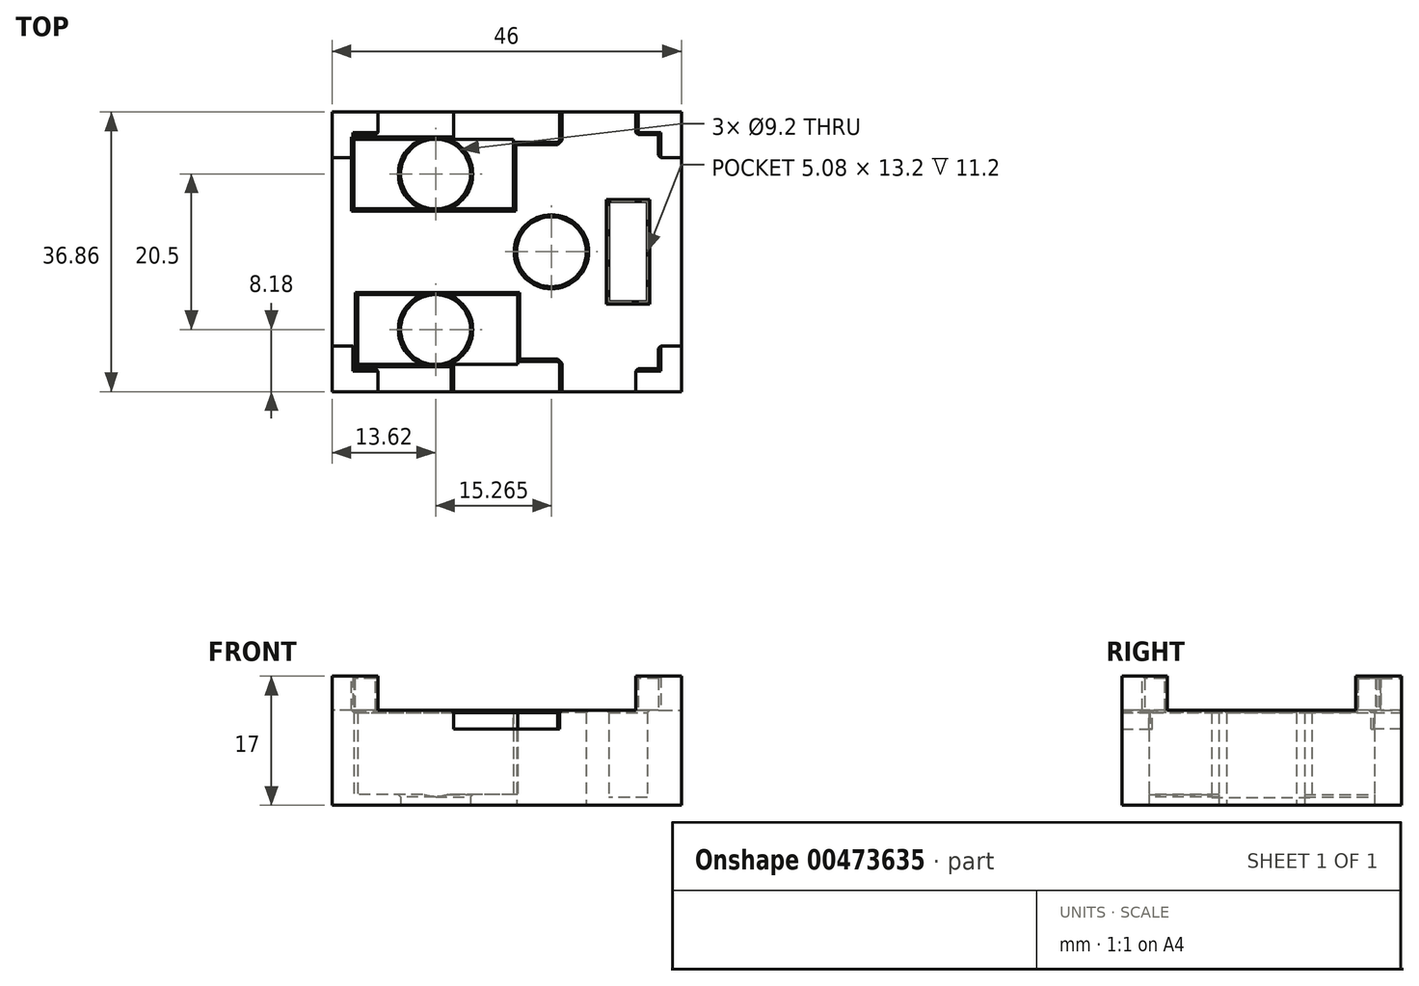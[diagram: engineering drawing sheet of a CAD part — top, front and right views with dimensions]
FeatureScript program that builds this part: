
annotation { "Feature Type Name" : "Feature", "Feature Type Description" : "" }
export const myFeature = defineFeature(function(context is Context, id is Id, definition is map)
    precondition{}
    {
        {
            var Q0;
            Q0=qCreatedBy(makeId("Top.planeOp"),FACE);
            var sketch = newSketch(context, id + "F0", { "sketchPlane" : qUnion([Q0])});
            skLineSegment(sketch, "E0.bottom", {"start": v(20, 15.43) * mm, "end": v(-20, 15.43) * mm});
            skLineSegment(sketch, "E0.top", {"start": v(20, -15.43) * mm, "end": v(-20, -15.43) * mm});
            skLineSegment(sketch, "E0.left", {"start": v(20, 15.43) * mm, "end": v(20, -15.43) * mm});
            skLineSegment(sketch, "E0.right", {"start": v(-20, 15.43) * mm, "end": v(-20, -15.43) * mm});
            skPoint(sketch, "E0.middle", {"position": v(0, 0) * mm});
            skLineSegment(sketch, "E1.0", {"start": v(-23, 18.43) * mm, "end": v(-23, -18.43) * mm});
            skLineSegment(sketch, "E1.1", {"start": v(23, 18.43) * mm, "end": v(-23, 18.43) * mm});
            skLineSegment(sketch, "E1.2", {"start": v(23, 18.43) * mm, "end": v(23, -18.43) * mm});
            skLineSegment(sketch, "E1.3", {"start": v(23, -18.43) * mm, "end": v(-23, -18.43) * mm});
            skLineSegment(sketch, "E2", {"start": v(-17, 15.43) * mm, "end": v(-17, 18.43) * mm});
            skLineSegment(sketch, "E3", {"start": v(17, 15.43) * mm, "end": v(17, 18.43) * mm});
            skLineSegment(sketch, "E4", {"start": v(20, 12.43) * mm, "end": v(23, 12.43) * mm});
            skLineSegment(sketch, "E5", {"start": v(-20, 12.43) * mm, "end": v(-23, 12.43) * mm});
            skLineSegment(sketch, "E6.MirrorCS", {"start": v(-20, -12.43) * mm, "end": v(-23, -12.43) * mm});
            skLineSegment(sketch, "E7.MirrorCS", {"start": v(-17, -15.43) * mm, "end": v(-17, -18.43) * mm});
            skLineSegment(sketch, "E8.MirrorCS", {"start": v(17, -15.43) * mm, "end": v(17, -18.43) * mm});
            skLineSegment(sketch, "E9.MirrorCS", {"start": v(20, -12.43) * mm, "end": v(23, -12.43) * mm});
            skLineSegment(sketch, "E10", {"start": v(-15, 10.25) * mm, "end": v(6.7, 10.25) * mm, "construction": true});
            skCircle(sketch, "E11", {"center": v(-17, 10.25) * mm, "radius": 1.03 * mm, "construction": true});
            skCircle(sketch, "E12", {"center": v(-11.92, 10.25) * mm, "radius": 1.03 * mm, "construction": true});
            skCircle(sketch, "E13", {"center": v(-6.84, 10.25) * mm, "radius": 1.03 * mm, "construction": true});
            skCircle(sketch, "E14", {"center": v(-1.76, 10.25) * mm, "radius": 1.03 * mm, "construction": true});
            skLineSegment(sketch, "E15.MirrorCS", {"start": v(-15, -10.25) * mm, "end": v(6.7, -10.25) * mm, "construction": true});
            skLineSegment(sketch, "E16.bottom", {"start": v(0.87, 5.65) * mm, "end": v(-19.63, 5.65) * mm});
            skLineSegment(sketch, "E16.top", {"start": v(0.87, 14.85) * mm, "end": v(-19.63, 14.85) * mm});
            skLineSegment(sketch, "E16.left", {"start": v(0.87, 5.65) * mm, "end": v(0.87, 14.85) * mm});
            skLineSegment(sketch, "E16.right", {"start": v(-19.63, 5.65) * mm, "end": v(-19.63, 14.85) * mm, "construction": true});
            skPoint(sketch, "E16.middle", {"position": v(-9.38, 10.25) * mm});
            skLineSegment(sketch, "E17.MirrorCS", {"start": v(0.87, -5.65) * mm, "end": v(0.87, -14.85) * mm, "construction": true});
            skLineSegment(sketch, "E18.MirrorCS", {"start": v(0.87, -14.85) * mm, "end": v(-19.63, -14.85) * mm});
            skLineSegment(sketch, "E19.MirrorCS", {"start": v(0.87, -5.65) * mm, "end": v(-19.63, -5.65) * mm});
            skLineSegment(sketch, "E20.MirrorCS", {"start": v(-19.63, -5.65) * mm, "end": v(-19.63, -14.85) * mm});
            skLineSegment(sketch, "E21", {"start": v(17.25, 11) * mm, "end": v(17.25, -11.34) * mm, "construction": true});
            skLineSegment(sketch, "E22.bottom", {"start": v(18.52, -6.6) * mm, "end": v(13.44, -6.6) * mm});
            skLineSegment(sketch, "E22.top", {"start": v(18.52, 6.6) * mm, "end": v(13.44, 6.6) * mm});
            skLineSegment(sketch, "E22.left", {"start": v(18.52, -6.6) * mm, "end": v(18.52, 6.6) * mm});
            skLineSegment(sketch, "E22.right", {"start": v(13.44, -6.6) * mm, "end": v(13.44, 6.6) * mm});
            skPoint(sketch, "E22.middle", {"position": v(15.98, 0) * mm});
            skLineSegment(sketch, "E23.bottom", {"start": v(-19.63, 14.85) * mm, "end": v(-20.18, 14.85) * mm});
            skLineSegment(sketch, "E23.top", {"start": v(-19.63, 5.65) * mm, "end": v(-20.18, 5.65) * mm});
            skLineSegment(sketch, "E23.left", {"start": v(-19.63, 14.85) * mm, "end": v(-19.63, 5.65) * mm, "construction": true});
            skLineSegment(sketch, "E23.right", {"start": v(-20.18, 14.85) * mm, "end": v(-20.18, 5.65) * mm});
            skLineSegment(sketch, "E24.bottom", {"start": v(0.87, -5.65) * mm, "end": v(1.42, -5.65) * mm});
            skLineSegment(sketch, "E24.top", {"start": v(0.87, -14.85) * mm, "end": v(1.42, -14.85) * mm});
            skLineSegment(sketch, "E24.right", {"start": v(1.42, -5.65) * mm, "end": v(1.42, -14.85) * mm});
            skCircle(sketch, "E25", {"center": v(-9.38, 10.25) * mm, "radius": 4.6 * mm});
            skCircle(sketch, "E26.MirrorC", {"center": v(-9.38, -10.25) * mm, "radius": 4.6 * mm});
            skCircle(sketch, "E27", {"center": v(5.89, 0) * mm, "radius": 4.6 * mm});
            skLineSegment(sketch, "E28", {"start": v(0.87, 5.65) * mm, "end": v(5.89, 0) * mm, "construction": true});
            skLineSegment(sketch, "E29", {"start": v(5.89, 0) * mm, "end": v(13.44, 0) * mm, "construction": true});
            skLineSegment(sketch, "E30", {"start": v(-7, 18.43) * mm, "end": v(-7, 15.43) * mm});
            skLineSegment(sketch, "E31.MirrorCS", {"start": v(7, 18.43) * mm, "end": v(7, 15.43) * mm});
            skLineSegment(sketch, "E32.MirrorCS", {"start": v(-7, -18.43) * mm, "end": v(-7, -15.43) * mm});
            skLineSegment(sketch, "E33.MirrorCS", {"start": v(7, -18.43) * mm, "end": v(7, -15.43) * mm});
            skSolve(sketch);
        }
        {
            var Q0;
            Q0=makeQuery(id+"F0.imprint","IMPRINT",FACE,{"disambiguationData":[TD([[makeQuery(id+"F0.imprint","IMPRINT",EDGE,{"derivedFrom":sQuery(id+"F0.wireOp",EDGE,"E16.bottom")}),1.0]])]});
            var Q1;
            {var subQ0=sQuery(id+"F0.wireOp",EDGE,"E2");Q1=makeQuery(id+"F0.imprint","IMPRINT",FACE,{"disambiguationData":[TD([[makeQuery(id+"F0.imprint","IMPRINT",EDGE,{"derivedFrom":subQ0}),-1.0]])]});}
            var Q2;
            {var subQ0=sQuery(id+"F0.wireOp",EDGE,"E6.MirrorCS");Q2=makeQuery(id+"F0.imprint","IMPRINT",FACE,{"disambiguationData":[TD([[makeQuery(id+"F0.imprint","IMPRINT",EDGE,{"derivedFrom":subQ0}),-1.0]])]});}
            var Q3;
            {var subQ0=sQuery(id+"F0.wireOp",EDGE,"E7.MirrorCS");Q3=makeQuery(id+"F0.imprint","IMPRINT",FACE,{"disambiguationData":[TD([[makeQuery(id+"F0.imprint","IMPRINT",EDGE,{"derivedFrom":subQ0}),1.0]])]});}
            var Q4;
            {var subQ0=sQuery(id+"F0.wireOp",EDGE,"E4");Q4=makeQuery(id+"F0.imprint","IMPRINT",FACE,{"disambiguationData":[TD([[makeQuery(id+"F0.imprint","IMPRINT",EDGE,{"derivedFrom":subQ0}),-1.0]])]});}
            var Q5;
            {var subQ0=sQuery(id+"F0.wireOp",EDGE,"E8.MirrorCS");Q5=makeQuery(id+"F0.imprint","IMPRINT",FACE,{"disambiguationData":[TD([[makeQuery(id+"F0.imprint","IMPRINT",EDGE,{"derivedFrom":subQ0}),-1.0]])]});}
            var Q6;
            {var subQ0=sQuery(id+"F0.wireOp",EDGE,"E3");Q6=makeQuery(id+"F0.imprint","IMPRINT",FACE,{"disambiguationData":[TD([[makeQuery(id+"F0.imprint","IMPRINT",EDGE,{"derivedFrom":subQ0}),1.0]])]});}
            var Q7;
            {var subQ0=sQuery(id+"F0.wireOp",EDGE,"E32.MirrorCS");Q7=makeQuery(id+"F0.imprint","IMPRINT",FACE,{"disambiguationData":[TD([[makeQuery(id+"F0.imprint","IMPRINT",EDGE,{"derivedFrom":subQ0}),-1.0]])]});}
            var Q8;
            {var subQ0=sQuery(id+"F0.wireOp",EDGE,"E30");Q8=makeQuery(id+"F0.imprint","IMPRINT",FACE,{"disambiguationData":[TD([[makeQuery(id+"F0.imprint","IMPRINT",EDGE,{"derivedFrom":subQ0}),1.0]])]});}
            extrude(context, id + "F1", {"entities" : qUnion([Q0, Q1, Q2, Q3, Q4, Q5, Q6, Q7, Q8]), "depth" : (15 - 2.5) * mm, "offsetDistance" : 25 * mm});
        }
        {
            var Q0;
            {var subQ5=sQuery(id+"F0.wireOp",EDGE,"E0.right");var subQ11=makeQuery(id+"F0.imprint","INTERSECT",VERTEX,{"derivedFrom":[subQ5,sQuery(id+"F0.wireOp",EDGE,"E5")]});Q0=makeQuery(id+"F0.imprint","IMPRINT",FACE,{"disambiguationData":[TD([[makeQuery(id+"F0.imprint","IMPRINT",EDGE,{"disambiguationData":[TD([[subQ11,1.0]])],"derivedFrom":subQ5}),1.0]])]});}
            var Q1;
            {var subQ0=sQuery(id+"F0.wireOp",EDGE,"E5");var subQ1=sQuery(id+"F0.wireOp",EDGE,"E0.right");var subQ2=makeQuery(id+"F0.imprint","INTERSECT",VERTEX,{"derivedFrom":[subQ1,subQ0]});Q1=makeQuery(id+"F0.imprint","IMPRINT",FACE,{"disambiguationData":[TD([[makeQuery(id+"F0.imprint","IMPRINT",EDGE,{"disambiguationData":[TD([[subQ2,-1.0]])],"derivedFrom":subQ1}),-1.0]])]});}
            var Q2;
            {var subQ0=sQuery(id+"F0.wireOp",EDGE,"E16.left");Q2=makeQuery(id+"F0.imprint","IMPRINT",FACE,{"disambiguationData":[TD([[makeQuery(id+"F0.imprint","IMPRINT",EDGE,{"derivedFrom":subQ0}),1.0]])]});}
            var Q3;
            {var subQ0=sQuery(id+"F0.wireOp",EDGE,"E20.MirrorCS");Q3=makeQuery(id+"F0.imprint","IMPRINT",FACE,{"disambiguationData":[TD([[makeQuery(id+"F0.imprint","IMPRINT",EDGE,{"derivedFrom":subQ0}),1.0]])]});}
            var Q4;
            {var subQ1=sQuery(id+"F0.wireOp",EDGE,"E24.bottom");Q4=makeQuery(id+"F0.imprint","IMPRINT",FACE,{"disambiguationData":[TD([[makeQuery(id+"F0.imprint","IMPRINT",EDGE,{"derivedFrom":subQ1}),-1.0]])]});}
            var Q5;
            {var subQ0=sQuery(id+"F0.wireOp",EDGE,"E5");var subQ1=sQuery(id+"F0.wireOp",EDGE,"E0.right");var subQ2=makeQuery(id+"F0.imprint","INTERSECT",VERTEX,{"derivedFrom":[subQ1,subQ0]});Q5=makeQuery(id+"F0.imprint","IMPRINT",FACE,{"disambiguationData":[TD([[makeQuery(id+"F0.imprint","IMPRINT",EDGE,{"disambiguationData":[TD([[subQ2,1.0]])],"derivedFrom":subQ1}),-1.0]])]});}
            extrude(context, id + "F2", {"entities" : qUnion([Q0, Q1, Q2, Q3, Q4, Q5]), "operationType" : NewBodyOperationType.ADD, "depth" : (15 - 13.6) * mm, "offsetDistance" : 25 * mm});
        }
        {
            var Q0;
            Q0=makeQuery(id+"F0.imprint","IMPRINT",FACE,{"disambiguationData":[TD([[makeQuery(id+"F0.imprint","IMPRINT",EDGE,{"derivedFrom":sQuery(id+"F0.wireOp",EDGE,"E22.bottom")}),-1.0]])]});
            extrude(context, id + "F3", {"entities" : qUnion([Q0]), "operationType" : NewBodyOperationType.ADD, "depth" : (15 - 14) * mm, "offsetDistance" : 25 * mm});
        }
        {
            var Q0;
            {var subQ3=sQuery(id+"F0.wireOp",EDGE,"E6.MirrorCS");Q0=makeQuery(id+"F0.imprint","IMPRINT",FACE,{"disambiguationData":[TD([[makeQuery(id+"F0.imprint","IMPRINT",EDGE,{"derivedFrom":subQ3}),1.0]])]});}
            var Q1;
            {var subQ4=sQuery(id+"F0.wireOp",EDGE,"E8.MirrorCS");Q1=makeQuery(id+"F0.imprint","IMPRINT",FACE,{"disambiguationData":[TD([[makeQuery(id+"F0.imprint","IMPRINT",EDGE,{"derivedFrom":subQ4}),1.0]])]});}
            var Q2;
            {var subQ3=sQuery(id+"F0.wireOp",EDGE,"E3");Q2=makeQuery(id+"F0.imprint","IMPRINT",FACE,{"disambiguationData":[TD([[makeQuery(id+"F0.imprint","IMPRINT",EDGE,{"derivedFrom":subQ3}),-1.0]])]});}
            var Q3;
            {var subQ3=sQuery(id+"F0.wireOp",EDGE,"E2");Q3=makeQuery(id+"F0.imprint","IMPRINT",FACE,{"disambiguationData":[TD([[makeQuery(id+"F0.imprint","IMPRINT",EDGE,{"derivedFrom":subQ3}),1.0]])]});}
            extrude(context, id + "F4", {"entities" : qUnion([Q0, Q1, Q2, Q3]), "operationType" : NewBodyOperationType.ADD, "depth" : 17 * mm, "offsetDistance" : 25 * mm});
        }
        {
            var Q0;
            Q0=makeQuery(id+"F1.opExtrude","CAP_FACE",FACE,{"disambiguationData":[OSD([sQuery(id+"F0.wireOp",EDGE,"E0.bottom"),sQuery(id+"F0.wireOp",EDGE,"E0.top"),sQuery(id+"F0.wireOp",EDGE,"E0.left"),sQuery(id+"F0.wireOp",EDGE,"E0.right"),sQuery(id+"F0.wireOp",EDGE,"E16.bottom"),sQuery(id+"F0.wireOp",EDGE,"E16.top"),sQuery(id+"F0.wireOp",EDGE,"E16.left"),sQuery(id+"F0.wireOp",EDGE,"E18.MirrorCS"),sQuery(id+"F0.wireOp",EDGE,"E19.MirrorCS"),sQuery(id+"F0.wireOp",EDGE,"E20.MirrorCS"),sQuery(id+"F0.wireOp",EDGE,"E22.bottom"),sQuery(id+"F0.wireOp",EDGE,"E22.top"),sQuery(id+"F0.wireOp",EDGE,"E22.left"),sQuery(id+"F0.wireOp",EDGE,"E22.right"),sQuery(id+"F0.wireOp",EDGE,"E23.bottom"),sQuery(id+"F0.wireOp",EDGE,"E23.top"),sQuery(id+"F0.wireOp",EDGE,"E24.bottom"),sQuery(id+"F0.wireOp",EDGE,"E24.top"),sQuery(id+"F0.wireOp",EDGE,"E24.right")])],"isStart":false});
            var sketch = newSketch(context, id + "F5", { "sketchPlane" : qUnion([Q0])});
            skLineSegment(sketch, "E34", {"start": v(0.87, 14.43) * mm, "end": v(20, 14.43) * mm});
            skLineSegment(sketch, "E35", {"start": v(1.42, -14.43) * mm, "end": v(20, -14.43) * mm});
            skLineSegment(sketch, "E36", {"start": v(-17, -5.65) * mm, "end": v(-17, 5.65) * mm});
            skLineSegment(sketch, "E37.0", {"start": v(7, -18.43) * mm, "end": v(7, -15.43) * mm});
            skLineSegment(sketch, "E37.1", {"start": v(-7, -18.43) * mm, "end": v(-7, -15.43) * mm});
            skLineSegment(sketch, "E37.2", {"start": v(7, 18.43) * mm, "end": v(7, 15.43) * mm});
            skLineSegment(sketch, "E37.3", {"start": v(-7, 18.43) * mm, "end": v(-7, 15.43) * mm});
            skLineSegment(sketch, "E38", {"start": v(-7, 15.43) * mm, "end": v(-7, 14.85) * mm});
            skLineSegment(sketch, "E39", {"start": v(7, 15.43) * mm, "end": v(7, 14.43) * mm});
            skLineSegment(sketch, "E40", {"start": v(-7, -15.43) * mm, "end": v(-7, -14.85) * mm});
            skLineSegment(sketch, "E41", {"start": v(7, -15.43) * mm, "end": v(7, -14.43) * mm});
            skSolve(sketch);
        }
        {
            var Q0;
            {var subQ2=sQuery(id+"F5.wireOp",EDGE,"E37.0");Q0=makeQuery(id+"F5.imprint","IMPRINT",FACE,{"disambiguationData":[TD([[makeQuery(id+"F5.imprint","IMPRINT",EDGE,{"derivedFrom":subQ2}),1.0]])]});}
            var Q1;
            {var subQ2=sQuery(id+"F5.wireOp",EDGE,"E37.2");Q1=makeQuery(id+"F5.imprint","IMPRINT",FACE,{"disambiguationData":[TD([[makeQuery(id+"F5.imprint","IMPRINT",EDGE,{"derivedFrom":subQ2}),-1.0]])]});}
            extrude(context, id + "F6", {"entities" : qUnion([Q0, Q1]), "operationType" : NewBodyOperationType.REMOVE, "oppositeDirection" : true, "depth" : 2.5 * mm, "offsetDistance" : 25 * mm});
        }
        {
            var Q0;
            Q0=makeQuery(id+"F1.opExtrude","CAP_EDGE",EDGE,{"disambiguationData":[OSD([sQuery(id+"F0.wireOp",EDGE,"E16.top"),sQuery(id+"F0.wireOp",EDGE,"E23.bottom")])],"isStart":false});
            var Q1;
            Q1=makeQuery(id+"F1.opExtrude","CAP_EDGE",EDGE,{"disambiguationData":[OSD([sQuery(id+"F0.wireOp",EDGE,"E23.right")])],"isStart":false});
            var Q2;
            Q2=makeQuery(id+"F1.opExtrude","CAP_EDGE",EDGE,{"disambiguationData":[OSD([sQuery(id+"F0.wireOp",EDGE,"E16.bottom"),sQuery(id+"F0.wireOp",EDGE,"E23.top")])],"isStart":false});
            var Q3;
            Q3=makeQuery(id+"F6.boolean.opBoolean","COPY",EDGE,{"derivedFrom":makeQuery(id+"F6.opExtrude","CAP_EDGE",EDGE,{"disambiguationData":[OSD([sQuery(id+"F0.wireOp",EDGE,"E16.bottom"),sQuery(id+"F0.wireOp",EDGE,"E23.top")])],"isStart":false})});
            var Q4;
            Q4=makeQuery(id+"F6.boolean.opBoolean","COPY",EDGE,{"derivedFrom":makeQuery(id+"F6.opExtrude","CAP_EDGE",EDGE,{"disambiguationData":[OSD([sQuery(id+"F0.wireOp",EDGE,"E16.left")])],"isStart":false})});
            var Q5;
            Q5=makeQuery(id+"F6.boolean.opBoolean","COPY",EDGE,{"derivedFrom":makeQuery(id+"F6.opExtrude","CAP_EDGE",EDGE,{"disambiguationData":[OSD([sQuery(id+"F0.wireOp",EDGE,"E22.left")])],"isStart":false})});
            var Q6;
            Q6=makeQuery(id+"F6.boolean.opBoolean","COPY",EDGE,{"derivedFrom":makeQuery(id+"F6.opExtrude","CAP_EDGE",EDGE,{"disambiguationData":[OSD([sQuery(id+"F0.wireOp",EDGE,"E22.top")])],"isStart":false})});
            var Q7;
            Q7=makeQuery(id+"F6.boolean.opBoolean","COPY",EDGE,{"derivedFrom":makeQuery(id+"F6.opExtrude","CAP_EDGE",EDGE,{"disambiguationData":[OSD([sQuery(id+"F0.wireOp",EDGE,"E22.right")])],"isStart":false})});
            var Q8;
            Q8=makeQuery(id+"F6.boolean.opBoolean","COPY",EDGE,{"derivedFrom":makeQuery(id+"F6.opExtrude","CAP_EDGE",EDGE,{"disambiguationData":[OSD([sQuery(id+"F0.wireOp",EDGE,"E22.bottom")])],"isStart":false})});
            var Q9;
            Q9=makeQuery(id+"F6.boolean.opBoolean","COPY",EDGE,{"derivedFrom":makeQuery(id+"F6.opExtrude","CAP_EDGE",EDGE,{"disambiguationData":[OSD([sQuery(id+"F0.wireOp",EDGE,"E19.MirrorCS"),sQuery(id+"F0.wireOp",EDGE,"E24.bottom")])],"isStart":false})});
            var Q10;
            Q10=makeQuery(id+"F1.opExtrude","CAP_EDGE",EDGE,{"disambiguationData":[OSD([sQuery(id+"F0.wireOp",EDGE,"E19.MirrorCS"),sQuery(id+"F0.wireOp",EDGE,"E24.bottom")])],"isStart":false});
            var Q11;
            Q11=makeQuery(id+"F1.opExtrude","CAP_EDGE",EDGE,{"disambiguationData":[OSD([sQuery(id+"F0.wireOp",EDGE,"E20.MirrorCS")])],"isStart":false});
            var Q12;
            Q12=makeQuery(id+"F1.opExtrude","CAP_EDGE",EDGE,{"disambiguationData":[OSD([sQuery(id+"F0.wireOp",EDGE,"E18.MirrorCS"),sQuery(id+"F0.wireOp",EDGE,"E24.top")])],"isStart":false});
            var Q13;
            Q13=makeQuery(id+"F1.opExtrude","CAP_EDGE",EDGE,{"disambiguationData":[OSD([sQuery(id+"F0.wireOp",EDGE,"E24.right")])],"isStart":false});
            var Q14;
            Q14=makeQuery(id+"F6.boolean.opBoolean","COPY",EDGE,{"derivedFrom":makeQuery(id+"F6.opExtrude","CAP_EDGE",EDGE,{"disambiguationData":[OSD([sQuery(id+"F0.wireOp",EDGE,"E24.right")])],"isStart":false})});
            var Q15;
            Q15=makeQuery(id+"F1.opExtrude","CAP_EDGE",EDGE,{"disambiguationData":[OSD([sQuery(id+"F0.wireOp",EDGE,"E16.left")])],"isStart":false});
            var Q16;
            Q16=makeQuery(id+"F4.opExtrude","CAP_EDGE",EDGE,{"disambiguationData":[OSD([sQuery(id+"F0.wireOp",EDGE,"E23.right")])],"isStart":false});
            var Q17;
            Q17=makeQuery(id+"F4.opExtrude","CAP_EDGE",EDGE,{"disambiguationData":[OSD([sQuery(id+"F0.wireOp",EDGE,"E23.bottom")])],"isStart":false});
            var Q18;
            Q18=makeQuery(id+"F4.opExtrude","SWEPT_EDGE",EDGE,{"disambiguationData":[OSD([sQuery(id+"F0.wireOp",EDGE,"E0.bottom"),sQuery(id+"F0.wireOp",EDGE,"E3")])]});
            var Q19;
            {var subQ0=sQuery(id+"F0.wireOp",EDGE,"E4");var subQ1=sQuery(id+"F0.wireOp",EDGE,"E0.left");Q19=makeQuery(id+"F6.boolean.opBoolean","MERGE",EDGE,{"derivedFrom":[makeQuery(id+"F4.opExtrude","SWEPT_EDGE",EDGE,{"disambiguationData":[OSD([subQ1,subQ0])]})],"fromTools":[makeQuery(id+"F6.opExtrude","SWEPT_EDGE",EDGE,{"disambiguationData":[OSD([subQ1,subQ0])]})]});}
            var Q20;
            Q20=makeQuery(id+"F4.opExtrude","SWEPT_EDGE",EDGE,{"disambiguationData":[OSD([sQuery(id+"F0.wireOp",EDGE,"E5"),sQuery(id+"F0.wireOp",EDGE,"E23.right")])]});
            var Q21;
            Q21=makeQuery(id+"F4.opExtrude","SWEPT_EDGE",EDGE,{"disambiguationData":[OSD([sQuery(id+"F0.wireOp",EDGE,"E0.bottom"),sQuery(id+"F0.wireOp",EDGE,"E2")])]});
            var Q22;
            Q22=makeQuery(id+"F4.opExtrude","SWEPT_EDGE",EDGE,{"disambiguationData":[OSD([sQuery(id+"F0.wireOp",EDGE,"E0.right"),sQuery(id+"F0.wireOp",EDGE,"E6.MirrorCS")])]});
            var Q23;
            Q23=makeQuery(id+"F4.opExtrude","SWEPT_EDGE",EDGE,{"disambiguationData":[OSD([sQuery(id+"F0.wireOp",EDGE,"E0.top"),sQuery(id+"F0.wireOp",EDGE,"E7.MirrorCS")])]});
            var Q24;
            {var subQ0=sQuery(id+"F0.wireOp",EDGE,"E9.MirrorCS");var subQ1=sQuery(id+"F0.wireOp",EDGE,"E0.left");Q24=makeQuery(id+"F6.boolean.opBoolean","MERGE",EDGE,{"derivedFrom":[makeQuery(id+"F4.opExtrude","SWEPT_EDGE",EDGE,{"disambiguationData":[OSD([subQ1,subQ0])]})],"fromTools":[makeQuery(id+"F6.opExtrude","SWEPT_EDGE",EDGE,{"disambiguationData":[OSD([subQ1,subQ0])]})]});}
            var Q25;
            Q25=makeQuery(id+"F4.opExtrude","SWEPT_EDGE",EDGE,{"disambiguationData":[OSD([sQuery(id+"F0.wireOp",EDGE,"E0.top"),sQuery(id+"F0.wireOp",EDGE,"E8.MirrorCS")])]});
            var Q26;
            {var subQ0=sQuery(id+"F0.wireOp",EDGE,"E25");Q26=makeQuery(id+"F2.opExtrude","CAP_EDGE",EDGE,{"disambiguationData":[OSD([subQ0]),TDD([makeQuery(id+"F0.imprint","IMPRINT",EDGE,{"disambiguationData":[TD([[makeQuery(id+"F0.imprint","INTERSECT",VERTEX,{"derivedFrom":[sQuery(id+"F0.wireOp",EDGE,"E16.bottom"),subQ0]}),1.0]])],"derivedFrom":subQ0})])],"isStart":false});}
            var Q27;
            {var subQ0=sQuery(id+"F0.wireOp",EDGE,"E26.MirrorC");Q27=makeQuery(id+"F2.opExtrude","CAP_EDGE",EDGE,{"disambiguationData":[OSD([subQ0]),TDD([makeQuery(id+"F0.imprint","IMPRINT",EDGE,{"disambiguationData":[TD([[makeQuery(id+"F0.imprint","INTERSECT",VERTEX,{"derivedFrom":[sQuery(id+"F0.wireOp",EDGE,"E18.MirrorCS"),subQ0]}),-1.0]])],"derivedFrom":subQ0})])],"isStart":false});}
            var Q28;
            Q28=makeQuery(id+"F6.boolean.opBoolean","COPY",EDGE,{"derivedFrom":makeQuery(id+"F6.opExtrude","CAP_EDGE",EDGE,{"disambiguationData":[OSD([sQuery(id+"F0.wireOp",EDGE,"E27")])],"isStart":false})});
            var Q29;
            Q29=makeQuery(id+"F6.boolean.opBoolean","COPY",EDGE,{"derivedFrom":makeQuery(id+"F6.opExtrude","CAP_EDGE",EDGE,{"disambiguationData":[OSD([sQuery(id+"F5.wireOp",EDGE,"E35")])],"isStart":true})});
            var Q30;
            Q30=makeQuery(id+"F6.boolean.opBoolean","COPY",EDGE,{"derivedFrom":makeQuery(id+"F6.opExtrude","CAP_EDGE",EDGE,{"disambiguationData":[OSD([sQuery(id+"F5.wireOp",EDGE,"E37.0"),sQuery(id+"F5.wireOp",EDGE,"E41")])],"isStart":true})});
            var Q31;
            Q31=makeQuery(id+"F6.boolean.opBoolean","COPY",EDGE,{"derivedFrom":makeQuery(id+"F6.opExtrude","CAP_EDGE",EDGE,{"disambiguationData":[OSD([sQuery(id+"F5.wireOp",EDGE,"E37.1"),sQuery(id+"F5.wireOp",EDGE,"E40")])],"isStart":true})});
            var Q32;
            Q32=makeQuery(id+"F6.boolean.opBoolean","COPY",EDGE,{"derivedFrom":makeQuery(id+"F6.opExtrude","CAP_EDGE",EDGE,{"disambiguationData":[OSD([sQuery(id+"F5.wireOp",EDGE,"E37.3"),sQuery(id+"F5.wireOp",EDGE,"E38")])],"isStart":true})});
            var Q33;
            Q33=makeQuery(id+"F6.boolean.opBoolean","COPY",EDGE,{"derivedFrom":makeQuery(id+"F6.opExtrude","CAP_EDGE",EDGE,{"disambiguationData":[OSD([sQuery(id+"F5.wireOp",EDGE,"E37.2"),sQuery(id+"F5.wireOp",EDGE,"E39")])],"isStart":true})});
            var Q34;
            Q34=makeQuery(id+"F6.boolean.opBoolean","COPY",EDGE,{"derivedFrom":makeQuery(id+"F6.opExtrude","CAP_EDGE",EDGE,{"disambiguationData":[OSD([sQuery(id+"F5.wireOp",EDGE,"E34")])],"isStart":true})});
            var Q35;
            Q35=makeQuery(id+"F6.boolean.opBoolean","COPY",EDGE,{"derivedFrom":makeQuery(id+"F6.opExtrude","CAP_EDGE",EDGE,{"disambiguationData":[OSD([sQuery(id+"F0.wireOp",EDGE,"E18.MirrorCS"),sQuery(id+"F0.wireOp",EDGE,"E24.top")])],"isStart":false})});
            var Q36;
            Q36=makeQuery(id+"F6.boolean.opBoolean","COPY",EDGE,{"derivedFrom":makeQuery(id+"F6.opExtrude","CAP_EDGE",EDGE,{"disambiguationData":[OSD([sQuery(id+"F0.wireOp",EDGE,"E16.top"),sQuery(id+"F0.wireOp",EDGE,"E23.bottom")])],"isStart":false})});
            var Q37;
            Q37=makeQuery(id+"F6.boolean.opBoolean","COPY",EDGE,{"derivedFrom":makeQuery(id+"F6.opExtrude","SWEPT_EDGE",EDGE,{"disambiguationData":[OSD([sQuery(id+"F0.wireOp",EDGE,"E16.top"),sQuery(id+"F0.wireOp",EDGE,"E23.bottom"),sQuery(id+"F5.wireOp",EDGE,"E38")])]})});
            var Q38;
            Q38=makeQuery(id+"F6.boolean.opBoolean","COPY",EDGE,{"derivedFrom":makeQuery(id+"F6.opExtrude","SWEPT_EDGE",EDGE,{"disambiguationData":[OSD([sQuery(id+"F0.wireOp",EDGE,"E18.MirrorCS"),sQuery(id+"F0.wireOp",EDGE,"E24.top"),sQuery(id+"F5.wireOp",EDGE,"E40")])]})});
            var Q39;
            Q39=makeQuery(id+"F6.boolean.opBoolean","COPY",EDGE,{"derivedFrom":makeQuery(id+"F6.opExtrude","SWEPT_EDGE",EDGE,{"disambiguationData":[OSD([sQuery(id+"F5.wireOp",EDGE,"E35"),sQuery(id+"F5.wireOp",EDGE,"E41")])]})});
            var Q40;
            Q40=makeQuery(id+"F6.boolean.opBoolean","COPY",EDGE,{"derivedFrom":makeQuery(id+"F6.opExtrude","SWEPT_EDGE",EDGE,{"disambiguationData":[OSD([sQuery(id+"F5.wireOp",EDGE,"E34"),sQuery(id+"F5.wireOp",EDGE,"E39")])]})});
            var Q41;
            {var subQ0=sQuery(id+"F0.wireOp",EDGE,"E0.bottom");Q41=makeQuery(id+"F4.opExtrude","CAP_EDGE",EDGE,{"disambiguationData":[OSD([subQ0]),TDD([makeQuery(id+"F0.imprint","IMPRINT",EDGE,{"disambiguationData":[TD([[makeQuery(id+"F0.imprint","INTERSECT",VERTEX,{"derivedFrom":[subQ0,sQuery(id+"F0.wireOp",EDGE,"E0.right")]}),1.0]])],"derivedFrom":subQ0})])],"isStart":false});}
            var Q42;
            Q42=makeQuery(id+"F4.opExtrude","CAP_EDGE",EDGE,{"disambiguationData":[OSD([sQuery(id+"F0.wireOp",EDGE,"E3")])],"isStart":false});
            var Q43;
            {var subQ0=sQuery(id+"F0.wireOp",EDGE,"E0.bottom");Q43=makeQuery(id+"F4.opExtrude","CAP_EDGE",EDGE,{"disambiguationData":[OSD([subQ0]),TDD([makeQuery(id+"F0.imprint","IMPRINT",EDGE,{"disambiguationData":[TD([[makeQuery(id+"F0.imprint","INTERSECT",VERTEX,{"derivedFrom":[subQ0,sQuery(id+"F0.wireOp",EDGE,"E0.left")]}),-1.0]])],"derivedFrom":subQ0})])],"isStart":false});}
            var Q44;
            {var subQ0=sQuery(id+"F0.wireOp",EDGE,"E0.left");Q44=makeQuery(id+"F4.opExtrude","CAP_EDGE",EDGE,{"disambiguationData":[OSD([subQ0]),TDD([makeQuery(id+"F0.imprint","IMPRINT",EDGE,{"disambiguationData":[TD([[makeQuery(id+"F0.imprint","INTERSECT",VERTEX,{"derivedFrom":[sQuery(id+"F0.wireOp",EDGE,"E0.bottom"),subQ0]}),-1.0]])],"derivedFrom":subQ0})])],"isStart":false});}
            var Q45;
            {var subQ0=sQuery(id+"F0.wireOp",EDGE,"E0.left");Q45=makeQuery(id+"F4.opExtrude","CAP_EDGE",EDGE,{"disambiguationData":[OSD([subQ0]),TDD([makeQuery(id+"F0.imprint","IMPRINT",EDGE,{"disambiguationData":[TD([[makeQuery(id+"F0.imprint","INTERSECT",VERTEX,{"derivedFrom":[sQuery(id+"F0.wireOp",EDGE,"E0.top"),subQ0]}),1.0]])],"derivedFrom":subQ0})])],"isStart":false});}
            var Q46;
            {var subQ0=sQuery(id+"F0.wireOp",EDGE,"E0.top");Q46=makeQuery(id+"F4.opExtrude","CAP_EDGE",EDGE,{"disambiguationData":[OSD([subQ0]),TDD([makeQuery(id+"F0.imprint","IMPRINT",EDGE,{"disambiguationData":[TD([[makeQuery(id+"F0.imprint","INTERSECT",VERTEX,{"derivedFrom":[subQ0,sQuery(id+"F0.wireOp",EDGE,"E0.left")]}),-1.0]])],"derivedFrom":subQ0})])],"isStart":false});}
            var Q47;
            {var subQ0=sQuery(id+"F0.wireOp",EDGE,"E0.top");Q47=makeQuery(id+"F4.opExtrude","CAP_EDGE",EDGE,{"disambiguationData":[OSD([subQ0]),TDD([makeQuery(id+"F0.imprint","IMPRINT",EDGE,{"disambiguationData":[TD([[makeQuery(id+"F0.imprint","INTERSECT",VERTEX,{"derivedFrom":[subQ0,sQuery(id+"F0.wireOp",EDGE,"E0.right")]}),1.0]])],"derivedFrom":subQ0})])],"isStart":false});}
            var Q48;
            {var subQ0=sQuery(id+"F0.wireOp",EDGE,"E0.right");Q48=makeQuery(id+"F4.opExtrude","CAP_EDGE",EDGE,{"disambiguationData":[OSD([subQ0]),TDD([makeQuery(id+"F0.imprint","IMPRINT",EDGE,{"disambiguationData":[TD([[makeQuery(id+"F0.imprint","INTERSECT",VERTEX,{"derivedFrom":[sQuery(id+"F0.wireOp",EDGE,"E0.top"),subQ0]}),1.0]])],"derivedFrom":subQ0})])],"isStart":false});}
            var Q49;
            {var subQ0=sQuery(id+"F0.wireOp",EDGE,"E0.right");Q49=makeQuery(id+"F4.opExtrude","CAP_EDGE",EDGE,{"disambiguationData":[OSD([subQ0]),TDD([makeQuery(id+"F0.imprint","IMPRINT",EDGE,{"disambiguationData":[TD([[makeQuery(id+"F0.imprint","INTERSECT",VERTEX,{"derivedFrom":[sQuery(id+"F0.wireOp",EDGE,"E0.bottom"),subQ0]}),-1.0]])],"derivedFrom":subQ0})])],"isStart":false});}
            var Q50;
            Q50=makeQuery(id+"F6.boolean.opBoolean","COPY",EDGE,{"derivedFrom":makeQuery(id+"F6.opExtrude","SWEPT_EDGE",EDGE,{"disambiguationData":[OSD([sQuery(id+"F0.wireOp",EDGE,"E19.MirrorCS"),sQuery(id+"F0.wireOp",EDGE,"E24.bottom"),sQuery(id+"F5.wireOp",EDGE,"E36")])]})});
            var Q51;
            Q51=makeQuery(id+"F6.boolean.opBoolean","COPY",EDGE,{"derivedFrom":makeQuery(id+"F6.opExtrude","SWEPT_EDGE",EDGE,{"disambiguationData":[OSD([sQuery(id+"F0.wireOp",EDGE,"E16.bottom"),sQuery(id+"F0.wireOp",EDGE,"E23.top"),sQuery(id+"F5.wireOp",EDGE,"E36")])]})});
            var Q52;
            Q52=makeQuery(id+"F1.opExtrude","CAP_EDGE",EDGE,{"disambiguationData":[OSD([sQuery(id+"F0.wireOp",EDGE,"E27")])],"isStart":false});
            var Q53;
            Q53=makeQuery(id+"F1.opExtrude","CAP_EDGE",EDGE,{"disambiguationData":[OSD([sQuery(id+"F0.wireOp",EDGE,"E22.right")])],"isStart":false});
            var Q54;
            Q54=makeQuery(id+"F1.opExtrude","CAP_EDGE",EDGE,{"disambiguationData":[OSD([sQuery(id+"F0.wireOp",EDGE,"E22.top")])],"isStart":false});
            var Q55;
            Q55=makeQuery(id+"F1.opExtrude","CAP_EDGE",EDGE,{"disambiguationData":[OSD([sQuery(id+"F0.wireOp",EDGE,"E22.left")])],"isStart":false});
            var Q56;
            Q56=makeQuery(id+"F1.opExtrude","CAP_EDGE",EDGE,{"disambiguationData":[OSD([sQuery(id+"F0.wireOp",EDGE,"E22.bottom")])],"isStart":false});
            chamfer(context, id + "F7", {"entities" : qUnion([Q0, Q1, Q2, Q3, Q4, Q5, Q6, Q7, Q8, Q9, Q10, Q11, Q12, Q13, Q14, Q15, Q16, Q17, Q18, Q19, Q20, Q21, Q22, Q23, Q24, Q25, Q26, Q27, Q28, Q29, Q30, Q31, Q32, Q33, Q34, Q35, Q36, Q37, Q38, Q39, Q40, Q41, Q42, Q43, Q44, Q45, Q46, Q47, Q48, Q49, Q50, Q51, Q52, Q53, Q54, Q55, Q56]), "width" : 0.3 * mm, "tangentPropagation" : true});
        }
        {
            var Q0;
            Q0=makeQuery(id+"F4.opExtrude","SWEPT_EDGE",EDGE,{"disambiguationData":[OSD([sQuery(id+"F0.wireOp",EDGE,"E0.right"),sQuery(id+"F0.wireOp",EDGE,"E23.bottom")])]});
            chamfer(context, id + "F8", {"entities" : qUnion([Q0]), "width" : 0.3 * mm, "tangentPropagation" : true});
        }
    });
